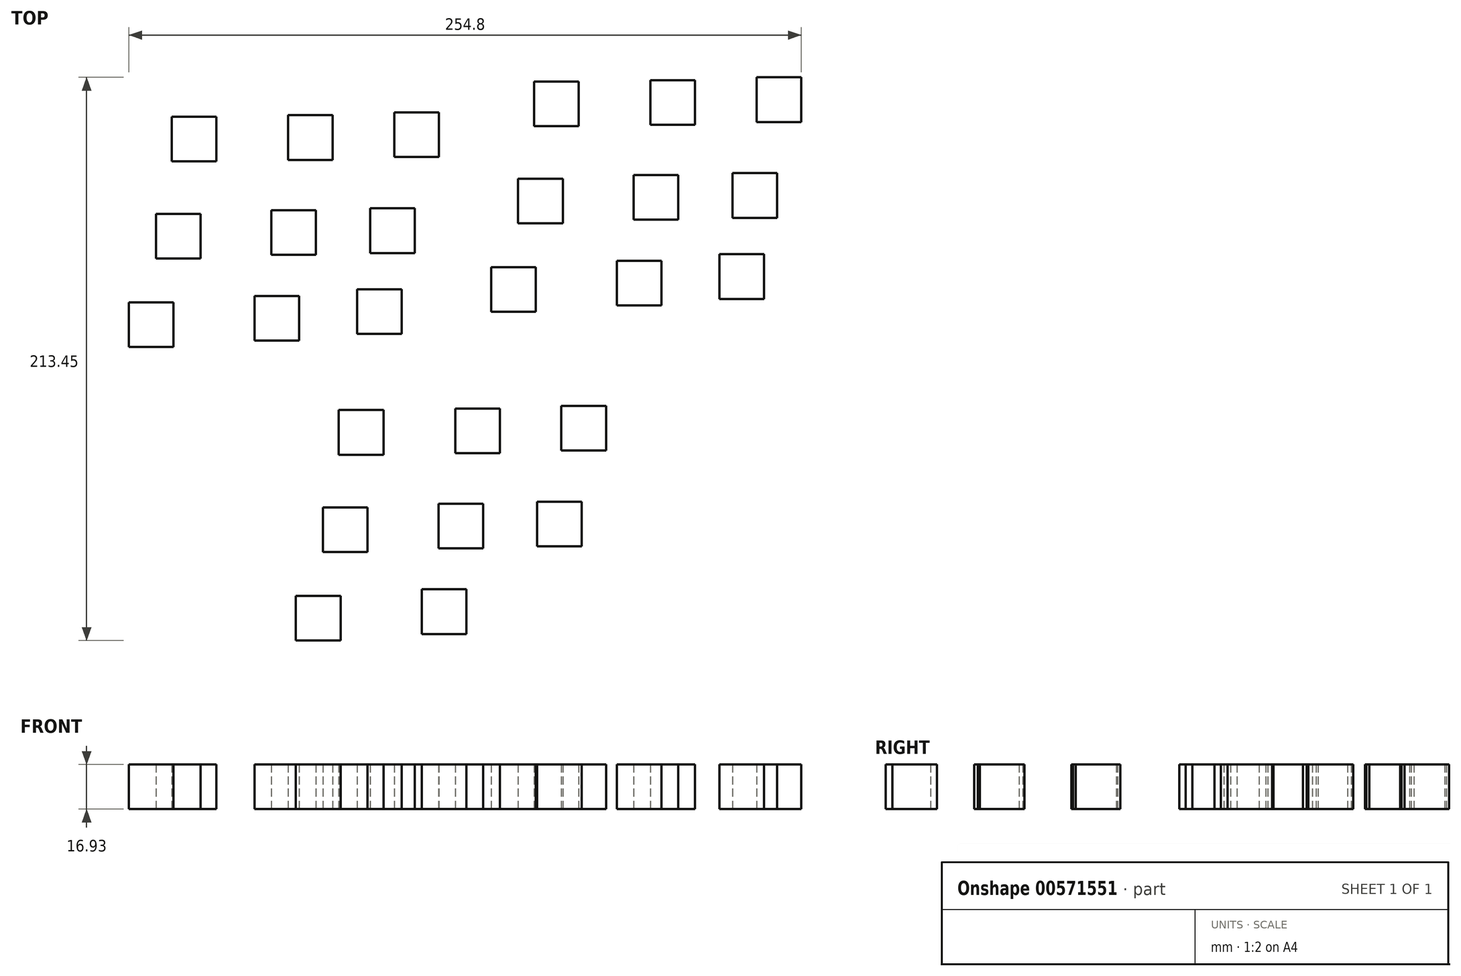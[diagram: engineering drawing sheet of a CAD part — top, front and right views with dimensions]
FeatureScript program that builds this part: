
annotation { "Feature Type Name" : "Feature", "Feature Type Description" : "" }
export const myFeature = defineFeature(function(context is Context, id is Id, definition is map)
    precondition{}
    {
        {
            var Q0;
            Q0=qCreatedBy(makeId("Top.planeOp"),FACE);
            var sketch = newSketch(context, id + "F0", { "sketchPlane" : qUnion([Q0])});
            skLineSegment(sketch, "E0.bottom", {"start": v(-54.7, 41.83) * mm, "end": v(-71.64, 41.83) * mm});
            skLineSegment(sketch, "E0.top", {"start": v(-54.7, 58.76) * mm, "end": v(-71.64, 58.76) * mm});
            skLineSegment(sketch, "E0.left", {"start": v(-54.7, 41.83) * mm, "end": v(-54.7, 58.76) * mm});
            skLineSegment(sketch, "E0.right", {"start": v(-71.64, 41.83) * mm, "end": v(-71.64, 58.76) * mm});
            skPoint(sketch, "E0.middle", {"position": v(-63.17, 50.3) * mm});
            skLineSegment(sketch, "E1.bottom", {"start": v(-10.6, 42.38) * mm, "end": v(-27.52, 42.38) * mm});
            skLineSegment(sketch, "E1.top", {"start": v(-10.6, 59.32) * mm, "end": v(-27.52, 59.32) * mm});
            skLineSegment(sketch, "E1.left", {"start": v(-10.6, 42.38) * mm, "end": v(-10.6, 59.32) * mm});
            skLineSegment(sketch, "E1.right", {"start": v(-27.52, 42.38) * mm, "end": v(-27.52, 59.32) * mm});
            skPoint(sketch, "E1.middle", {"position": v(-19.06, 50.85) * mm});
            skLineSegment(sketch, "E2.bottom", {"start": v(29.64, 43.44) * mm, "end": v(12.7, 43.44) * mm});
            skLineSegment(sketch, "E2.top", {"start": v(29.64, 60.38) * mm, "end": v(12.7, 60.38) * mm});
            skLineSegment(sketch, "E2.left", {"start": v(29.64, 43.44) * mm, "end": v(29.64, 60.38) * mm});
            skLineSegment(sketch, "E2.right", {"start": v(12.7, 43.44) * mm, "end": v(12.7, 60.38) * mm});
            skPoint(sketch, "E2.middle", {"position": v(21.17, 51.91) * mm});
            skLineSegment(sketch, "E3.bottom", {"start": v(-60.7, 4.98) * mm, "end": v(-77.64, 4.98) * mm});
            skLineSegment(sketch, "E3.top", {"start": v(-60.7, 21.9) * mm, "end": v(-77.64, 21.9) * mm});
            skLineSegment(sketch, "E3.left", {"start": v(-60.7, 4.98) * mm, "end": v(-60.7, 21.9) * mm});
            skLineSegment(sketch, "E3.right", {"start": v(-77.64, 4.98) * mm, "end": v(-77.64, 21.9) * mm});
            skPoint(sketch, "E3.middle", {"position": v(-69.17, 13.44) * mm});
            skLineSegment(sketch, "E4.bottom", {"start": v(-16.94, 6.39) * mm, "end": v(-33.88, 6.39) * mm});
            skLineSegment(sketch, "E4.top", {"start": v(-16.94, 23.32) * mm, "end": v(-33.88, 23.32) * mm});
            skLineSegment(sketch, "E4.left", {"start": v(-16.94, 6.39) * mm, "end": v(-16.94, 23.32) * mm});
            skLineSegment(sketch, "E4.right", {"start": v(-33.88, 6.39) * mm, "end": v(-33.88, 23.32) * mm});
            skPoint(sketch, "E4.middle", {"position": v(-25.41, 14.85) * mm});
            skLineSegment(sketch, "E5.bottom", {"start": v(20.47, 7.1) * mm, "end": v(3.53, 7.1) * mm});
            skLineSegment(sketch, "E5.top", {"start": v(20.47, 24.03) * mm, "end": v(3.53, 24.03) * mm});
            skLineSegment(sketch, "E5.left", {"start": v(20.47, 7.1) * mm, "end": v(20.47, 24.03) * mm});
            skLineSegment(sketch, "E5.right", {"start": v(3.53, 7.1) * mm, "end": v(3.53, 24.03) * mm});
            skPoint(sketch, "E5.middle", {"position": v(12, 15.56) * mm});
            skLineSegment(sketch, "E6.bottom", {"start": v(-70.94, -28.55) * mm, "end": v(-87.87, -28.55) * mm});
            skLineSegment(sketch, "E6.top", {"start": v(-70.94, -11.62) * mm, "end": v(-87.87, -11.62) * mm});
            skLineSegment(sketch, "E6.left", {"start": v(-70.94, -28.55) * mm, "end": v(-70.94, -11.62) * mm});
            skLineSegment(sketch, "E6.right", {"start": v(-87.87, -28.55) * mm, "end": v(-87.87, -11.62) * mm});
            skPoint(sketch, "E6.middle", {"position": v(-79.4, -20.09) * mm});
            skLineSegment(sketch, "E7.bottom", {"start": v(-23.3, -26.08) * mm, "end": v(-40.23, -26.08) * mm});
            skLineSegment(sketch, "E7.top", {"start": v(-23.3, -9.15) * mm, "end": v(-40.23, -9.15) * mm});
            skLineSegment(sketch, "E7.left", {"start": v(-23.3, -26.08) * mm, "end": v(-23.3, -9.15) * mm});
            skLineSegment(sketch, "E7.right", {"start": v(-40.23, -26.08) * mm, "end": v(-40.23, -9.15) * mm});
            skPoint(sketch, "E7.middle", {"position": v(-31.76, -17.62) * mm});
            skLineSegment(sketch, "E8.bottom", {"start": v(15.52, -23.61) * mm, "end": v(-1.4, -23.61) * mm});
            skLineSegment(sketch, "E8.top", {"start": v(15.52, -6.68) * mm, "end": v(-1.4, -6.68) * mm});
            skLineSegment(sketch, "E8.left", {"start": v(15.52, -23.61) * mm, "end": v(15.52, -6.68) * mm});
            skLineSegment(sketch, "E8.right", {"start": v(-1.4, -23.61) * mm, "end": v(-1.4, -6.68) * mm});
            skPoint(sketch, "E8.middle", {"position": v(7.06, -15.14) * mm});
            skLineSegment(sketch, "E9.bottom", {"start": v(82.58, 55.15) * mm, "end": v(65.65, 55.15) * mm});
            skLineSegment(sketch, "E9.top", {"start": v(82.58, 72.08) * mm, "end": v(65.65, 72.08) * mm});
            skLineSegment(sketch, "E9.left", {"start": v(82.58, 55.15) * mm, "end": v(82.58, 72.08) * mm});
            skLineSegment(sketch, "E9.right", {"start": v(65.65, 55.15) * mm, "end": v(65.65, 72.08) * mm});
            skPoint(sketch, "E9.middle", {"position": v(74.11, 63.61) * mm});
            skLineSegment(sketch, "E10.bottom", {"start": v(126.7, 55.7) * mm, "end": v(109.76, 55.7) * mm});
            skLineSegment(sketch, "E10.top", {"start": v(126.7, 72.63) * mm, "end": v(109.76, 72.63) * mm});
            skLineSegment(sketch, "E10.left", {"start": v(126.7, 55.7) * mm, "end": v(126.7, 72.63) * mm});
            skLineSegment(sketch, "E10.right", {"start": v(109.76, 55.7) * mm, "end": v(109.76, 72.63) * mm});
            skPoint(sketch, "E10.middle", {"position": v(118.23, 64.17) * mm});
            skLineSegment(sketch, "E11.bottom", {"start": v(166.93, 56.76) * mm, "end": v(150, 56.76) * mm});
            skLineSegment(sketch, "E11.top", {"start": v(166.93, 73.7) * mm, "end": v(150, 73.7) * mm});
            skLineSegment(sketch, "E11.left", {"start": v(166.93, 56.76) * mm, "end": v(166.93, 73.7) * mm});
            skLineSegment(sketch, "E11.right", {"start": v(150, 56.76) * mm, "end": v(150, 73.7) * mm});
            skPoint(sketch, "E11.middle", {"position": v(158.46, 65.23) * mm});
            skLineSegment(sketch, "E12.bottom", {"start": v(76.58, 18.3) * mm, "end": v(59.65, 18.3) * mm});
            skLineSegment(sketch, "E12.top", {"start": v(76.58, 35.22) * mm, "end": v(59.65, 35.22) * mm});
            skLineSegment(sketch, "E12.left", {"start": v(76.58, 18.3) * mm, "end": v(76.58, 35.22) * mm});
            skLineSegment(sketch, "E12.right", {"start": v(59.65, 18.3) * mm, "end": v(59.65, 35.22) * mm});
            skPoint(sketch, "E12.middle", {"position": v(68.11, 26.76) * mm});
            skLineSegment(sketch, "E13.bottom", {"start": v(120.34, 19.7) * mm, "end": v(103.4, 19.7) * mm});
            skLineSegment(sketch, "E13.top", {"start": v(120.34, 36.64) * mm, "end": v(103.4, 36.64) * mm});
            skLineSegment(sketch, "E13.left", {"start": v(120.34, 19.7) * mm, "end": v(120.34, 36.64) * mm});
            skLineSegment(sketch, "E13.right", {"start": v(103.4, 19.7) * mm, "end": v(103.4, 36.64) * mm});
            skPoint(sketch, "E13.middle", {"position": v(111.88, 28.17) * mm});
            skLineSegment(sketch, "E14.bottom", {"start": v(157.75, 20.4) * mm, "end": v(140.82, 20.4) * mm});
            skLineSegment(sketch, "E14.top", {"start": v(157.75, 37.34) * mm, "end": v(140.82, 37.34) * mm});
            skLineSegment(sketch, "E14.left", {"start": v(157.75, 20.4) * mm, "end": v(157.75, 37.34) * mm});
            skLineSegment(sketch, "E14.right", {"start": v(140.82, 20.4) * mm, "end": v(140.82, 37.34) * mm});
            skPoint(sketch, "E14.middle", {"position": v(149.28, 28.88) * mm});
            skLineSegment(sketch, "E15.bottom", {"start": v(66.35, -15.24) * mm, "end": v(49.41, -15.24) * mm});
            skLineSegment(sketch, "E15.top", {"start": v(66.35, 1.7) * mm, "end": v(49.41, 1.7) * mm});
            skLineSegment(sketch, "E15.left", {"start": v(66.35, -15.24) * mm, "end": v(66.35, 1.7) * mm});
            skLineSegment(sketch, "E15.right", {"start": v(49.41, -15.24) * mm, "end": v(49.41, 1.7) * mm});
            skPoint(sketch, "E15.middle", {"position": v(57.88, -6.77) * mm});
            skLineSegment(sketch, "E16.bottom", {"start": v(113.99, -12.77) * mm, "end": v(97.06, -12.77) * mm});
            skLineSegment(sketch, "E16.top", {"start": v(113.99, 4.17) * mm, "end": v(97.06, 4.17) * mm});
            skLineSegment(sketch, "E16.left", {"start": v(113.99, -12.77) * mm, "end": v(113.99, 4.17) * mm});
            skLineSegment(sketch, "E16.right", {"start": v(97.06, -12.77) * mm, "end": v(97.06, 4.17) * mm});
            skPoint(sketch, "E16.middle", {"position": v(105.52, -4.3) * mm});
            skLineSegment(sketch, "E17.bottom", {"start": v(152.81, -10.3) * mm, "end": v(135.88, -10.3) * mm});
            skLineSegment(sketch, "E17.top", {"start": v(152.81, 6.64) * mm, "end": v(135.88, 6.64) * mm});
            skLineSegment(sketch, "E17.left", {"start": v(152.81, -10.3) * mm, "end": v(152.81, 6.64) * mm});
            skLineSegment(sketch, "E17.right", {"start": v(135.88, -10.3) * mm, "end": v(135.88, 6.64) * mm});
            skPoint(sketch, "E17.middle", {"position": v(144.34, -1.83) * mm});
            skLineSegment(sketch, "E18.bottom", {"start": v(8.6, -69.38) * mm, "end": v(-8.34, -69.38) * mm});
            skLineSegment(sketch, "E18.top", {"start": v(8.6, -52.45) * mm, "end": v(-8.34, -52.45) * mm});
            skLineSegment(sketch, "E18.left", {"start": v(8.6, -69.38) * mm, "end": v(8.6, -52.45) * mm});
            skLineSegment(sketch, "E18.right", {"start": v(-8.34, -69.38) * mm, "end": v(-8.34, -52.45) * mm});
            skPoint(sketch, "E18.middle", {"position": v(0.12, -60.91) * mm});
            skLineSegment(sketch, "E19.bottom", {"start": v(52.7, -68.83) * mm, "end": v(35.77, -68.83) * mm});
            skLineSegment(sketch, "E19.top", {"start": v(52.7, -51.9) * mm, "end": v(35.77, -51.9) * mm});
            skLineSegment(sketch, "E19.left", {"start": v(52.7, -68.83) * mm, "end": v(52.7, -51.9) * mm});
            skLineSegment(sketch, "E19.right", {"start": v(35.77, -68.83) * mm, "end": v(35.77, -51.9) * mm});
            skPoint(sketch, "E19.middle", {"position": v(44.24, -60.36) * mm});
            skLineSegment(sketch, "E20.bottom", {"start": v(92.94, -67.77) * mm, "end": v(76, -67.77) * mm});
            skLineSegment(sketch, "E20.top", {"start": v(92.94, -50.83) * mm, "end": v(76, -50.83) * mm});
            skLineSegment(sketch, "E20.left", {"start": v(92.94, -67.77) * mm, "end": v(92.94, -50.83) * mm});
            skLineSegment(sketch, "E20.right", {"start": v(76, -67.77) * mm, "end": v(76, -50.83) * mm});
            skPoint(sketch, "E20.middle", {"position": v(84.47, -59.3) * mm});
            skLineSegment(sketch, "E21.bottom", {"start": v(2.6, -106.24) * mm, "end": v(-14.34, -106.24) * mm});
            skLineSegment(sketch, "E21.top", {"start": v(2.6, -89.3) * mm, "end": v(-14.34, -89.3) * mm});
            skLineSegment(sketch, "E21.left", {"start": v(2.6, -106.24) * mm, "end": v(2.6, -89.3) * mm});
            skLineSegment(sketch, "E21.right", {"start": v(-14.34, -106.24) * mm, "end": v(-14.34, -89.3) * mm});
            skPoint(sketch, "E21.middle", {"position": v(-5.88, -97.77) * mm});
            skLineSegment(sketch, "E22.bottom", {"start": v(46.35, -104.82) * mm, "end": v(29.42, -104.82) * mm});
            skLineSegment(sketch, "E22.top", {"start": v(46.35, -87.89) * mm, "end": v(29.42, -87.89) * mm});
            skLineSegment(sketch, "E22.left", {"start": v(46.35, -104.82) * mm, "end": v(46.35, -87.89) * mm});
            skLineSegment(sketch, "E22.right", {"start": v(29.42, -104.82) * mm, "end": v(29.42, -87.89) * mm});
            skPoint(sketch, "E22.middle", {"position": v(37.89, -96.36) * mm});
            skLineSegment(sketch, "E23.bottom", {"start": v(83.76, -104.12) * mm, "end": v(66.83, -104.12) * mm});
            skLineSegment(sketch, "E23.top", {"start": v(83.76, -87.18) * mm, "end": v(66.83, -87.18) * mm});
            skLineSegment(sketch, "E23.left", {"start": v(83.76, -104.12) * mm, "end": v(83.76, -87.18) * mm});
            skLineSegment(sketch, "E23.right", {"start": v(66.83, -104.12) * mm, "end": v(66.83, -87.18) * mm});
            skPoint(sketch, "E23.middle", {"position": v(75.3, -95.65) * mm});
            skLineSegment(sketch, "E24.bottom", {"start": v(-7.64, -139.76) * mm, "end": v(-24.58, -139.76) * mm});
            skLineSegment(sketch, "E24.top", {"start": v(-7.64, -122.83) * mm, "end": v(-24.58, -122.83) * mm});
            skLineSegment(sketch, "E24.left", {"start": v(-7.64, -139.76) * mm, "end": v(-7.64, -122.83) * mm});
            skLineSegment(sketch, "E24.right", {"start": v(-24.58, -139.76) * mm, "end": v(-24.58, -122.83) * mm});
            skPoint(sketch, "E24.middle", {"position": v(-16.1, -131.3) * mm});
            skLineSegment(sketch, "E25.bottom", {"start": v(40, -137.3) * mm, "end": v(23.07, -137.3) * mm});
            skLineSegment(sketch, "E25.top", {"start": v(40, -120.36) * mm, "end": v(23.07, -120.36) * mm});
            skLineSegment(sketch, "E25.left", {"start": v(40, -137.3) * mm, "end": v(40, -120.36) * mm});
            skLineSegment(sketch, "E25.right", {"start": v(23.07, -137.3) * mm, "end": v(23.07, -120.36) * mm});
            skPoint(sketch, "E25.middle", {"position": v(31.53, -128.83) * mm});
            skSolve(sketch);
        }
        {
            var Q0;
            Q0 = qSketchRegion(id + "F0", true);
            extrude(context, id + "F1", {"entities" : qUnion([Q0]), "depth" : 16.93 * mm, "offsetDistance" : 25.4 * mm});
        }
    });
